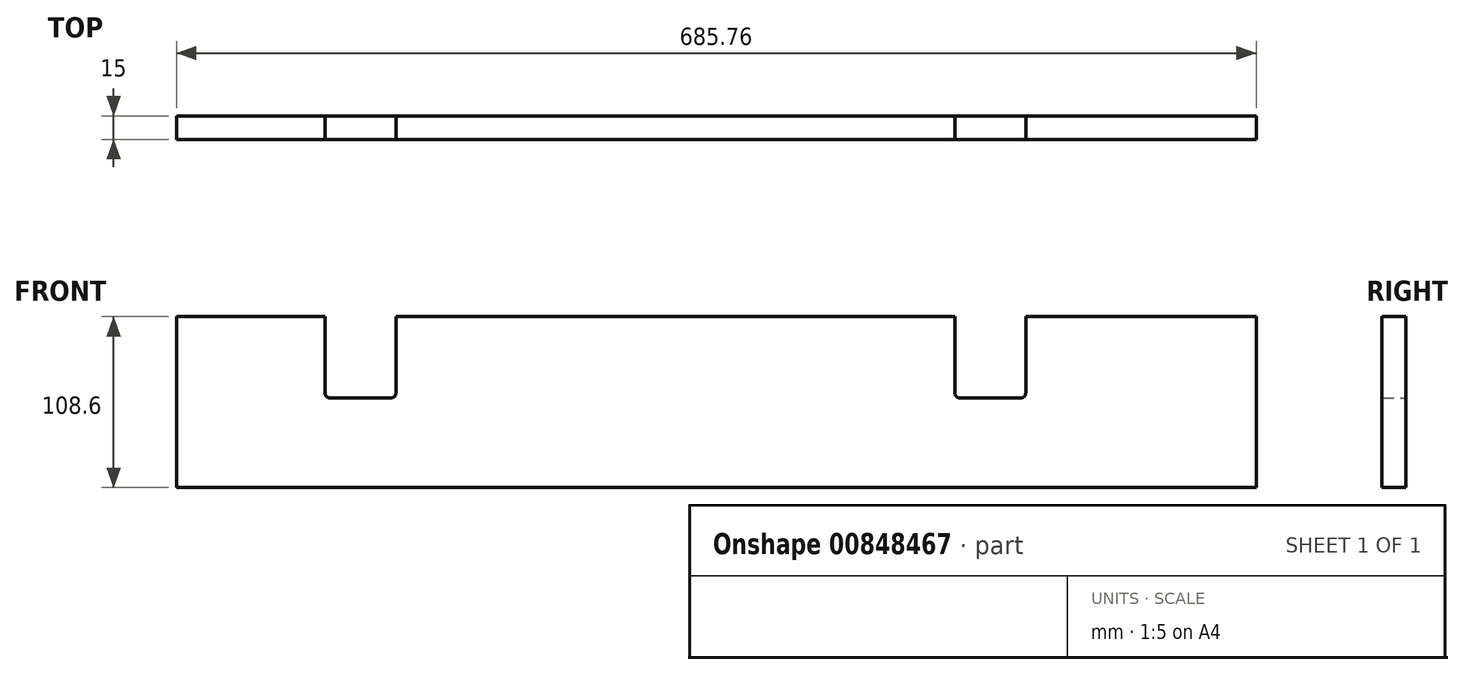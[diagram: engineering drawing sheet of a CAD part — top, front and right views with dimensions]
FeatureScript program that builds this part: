
annotation { "Feature Type Name" : "Feature", "Feature Type Description" : "" }
export const myFeature = defineFeature(function(context is Context, id is Id, definition is map)
    precondition{}
    {
        {
            var Q0;
            Q0=qCreatedBy(makeId("Top.planeOp"),FACE);
            var sketch = newSketch(context, id + "F0", { "sketchPlane" : qUnion([Q0])});
            skLineSegment(sketch, "E0.top", {"start": v(0, -7.5) * mm, "end": v(342.88, -7.5) * mm});
            skLineSegment(sketch, "E0.right", {"start": v(342.88, 7.5) * mm, "end": v(342.88, -7.5) * mm});
            skLineSegment(sketch, "E1", {"start": v(0, 7.5) * mm, "end": v(0, -7.5) * mm});
            skLineSegment(sketch, "E2", {"start": v(342.88, 7.5) * mm, "end": v(0, 7.5) * mm});
            skSolve(sketch);
        }
        {
            var Q0;
            Q0=makeQuery(id+"F0.imprint","IMPRINT",FACE,{"disambiguationData":[TD([[makeQuery(id+"F0.imprint","IMPRINT",EDGE,{"derivedFrom":sQuery(id+"F0.wireOp",EDGE,"E0.top")}),1.0]])]});
            extrude(context, id + "F1", {"entities" : qUnion([Q0]), "endBound" : BoundingType.SYMMETRIC, "depth" : 108.6 * mm, "offsetDistance" : 25 * mm});
        }
        {
            var Q0;
            Q0=makeQuery(id+"F1.opExtrude","SWEPT_BODY",BODY,{"disambiguationData":[OSD([sQuery(id+"F0.wireOp",EDGE,"E0.top"),sQuery(id+"F0.wireOp",EDGE,"E0.right"),sQuery(id+"F0.wireOp",EDGE,"E1"),sQuery(id+"F0.wireOp",EDGE,"FrvZOWco-Ps3S-NngT-Pmlh-8CwQ84urIFap"),sQuery(id+"F0.wireOp",EDGE,"ZoadJ8Hn-1iSU-lgYo-nJBm-p1Qox0YXjOP3"),sQuery(id+"F0.wireOp",EDGE,"neUbqu5C-sZVH-Du6l-Kckr-jQ0ifP0jSSAA"),sQuery(id+"F0.wireOp",EDGE,"q1D6MIjY-mNE6-asy1-L8oi-20T1G9Pd0vwO"),sQuery(id+"F0.wireOp",EDGE,"5SXKlSgM-nki9-3PKp-S8L6-EQkEBukCnOSp")])]});
            var Q1;
            Q1=makeQuery(id+"F1.opExtrude","SWEPT_FACE",FACE,{"disambiguationData":[OSD([sQuery(id+"F0.wireOp",EDGE,"E1")])]});
            mirror(context, id + "F2", {"operationType" : NewBodyOperationType.ADD, "entities" : qUnion([Q0]), "mirrorPlane" : qUnion([Q1])});
        }
        {
            var Q0;
            {var subQ0=makeQuery(id+"F1.opExtrude","SWEPT_FACE",FACE,{"disambiguationData":[OSD([sQuery(id+"F0.wireOp",EDGE,"E2")])]});Q0=makeQuery(id+"F2.boolean.opBoolean","MERGE",FACE,{"derivedFrom":[subQ0,makeQuery(id+"F2.opPattern","COPY",FACE,{"derivedFrom":subQ0,"instanceName":"1"})]});}
            var sketch = newSketch(context, id + "F3", { "sketchPlane" : qUnion([Q0])});
            skLineSegment(sketch, "E3.bottom", {"start": v(-196.5, 54.3) * mm, "end": v(-151.5, 54.3) * mm});
            skLineSegment(sketch, "E4.bottom", {"start": v(203.5, 54.3) * mm, "end": v(248.5, 54.3) * mm});
            skLineSegment(sketch, "E5", {"start": v(0, 87.4) * mm, "end": v(0, -77.3) * mm, "construction": true});
            skLineSegment(sketch, "E6", {"start": v(248.5, 54.3) * mm, "end": v(248.5, 5.7) * mm});
            skArc(sketch, "E7", {"start": v(248.5, 5.7) * mm, "mid": v(247.62, 3.58) * mm, "end": v(245.5, 2.7) * mm});
            skLineSegment(sketch, "E8", {"start": v(245.5, 2.7) * mm, "end": v(206.5, 2.7) * mm});
            skLineSegment(sketch, "E9", {"start": v(203.5, 54.3) * mm, "end": v(203.5, 5.7) * mm});
            skArc(sketch, "E10", {"start": v(206.5, 2.7) * mm, "mid": v(204.38, 3.58) * mm, "end": v(203.5, 5.7) * mm});
            skLineSegment(sketch, "E11", {"start": v(-151.5, 54.3) * mm, "end": v(-151.5, 5.7) * mm});
            skLineSegment(sketch, "E12", {"start": v(-196.5, 54.3) * mm, "end": v(-196.5, 5.7) * mm});
            skArc(sketch, "E13", {"start": v(-151.5, 5.7) * mm, "mid": v(-152.38, 3.58) * mm, "end": v(-154.5, 2.7) * mm});
            skLineSegment(sketch, "E14", {"start": v(-154.5, 2.7) * mm, "end": v(-193.5, 2.7) * mm});
            skArc(sketch, "E15", {"start": v(-193.5, 2.7) * mm, "mid": v(-195.62, 3.58) * mm, "end": v(-196.5, 5.7) * mm});
            skSolve(sketch);
        }
        {
            var Q0;
            Q0=qSketchRegion(id+"F3",true);
            extrude(context, id + "F4", {"entities" : qUnion([Q0]), "operationType" : NewBodyOperationType.REMOVE, "endBound" : BoundingType.UP_TO_NEXT, "oppositeDirection" : true, "depth" : 25 * mm, "offsetDistance" : 25 * mm});
        }
        {
            var Q0;
            Q0=qCreatedBy(makeId("Front.planeOp"),FACE);
            cPlane(context, id + "F5", {"entities" : qUnion([Q0]), "cplaneType" : CPlaneType.OFFSET, "offset" : 25 * mm, "width" : 150 * mm, "height" : 150 * mm});
        }
    });
